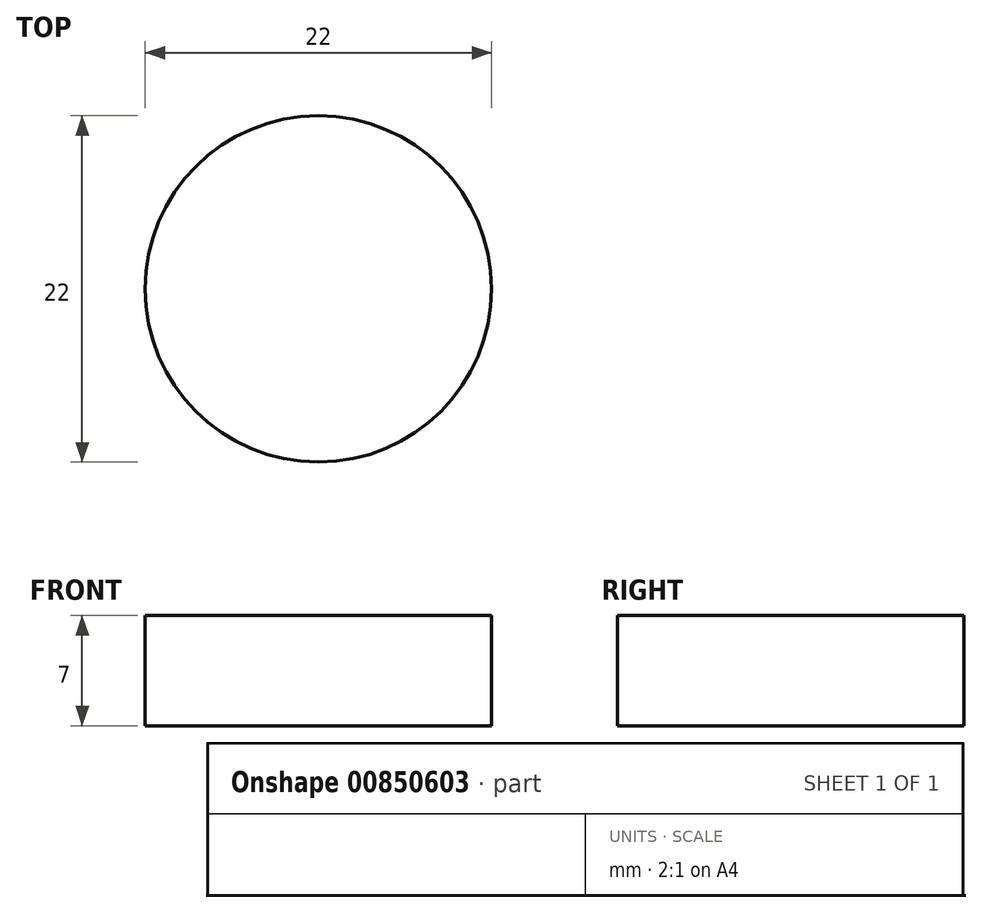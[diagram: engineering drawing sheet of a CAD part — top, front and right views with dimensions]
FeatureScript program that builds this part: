
annotation { "Feature Type Name" : "Feature", "Feature Type Description" : "" }
export const myFeature = defineFeature(function(context is Context, id is Id, definition is map)
    precondition{}
    {
        {
            var Q0;
            Q0=qCreatedBy(makeId("Top.planeOp"),FACE);
            var sketch = newSketch(context, id + "F0", { "sketchPlane" : qUnion([Q0])});
            skCircle(sketch, "E0", {"center": v(2.2, 0) * mm, "radius": 11 * mm});
            skSolve(sketch);
        }
        {
            var Q0;
            Q0 = qSketchRegion(id + "F0", true);
            extrude(context, id + "F1", {"entities" : qUnion([Q0]), "depth" : 7 * mm, "offsetDistance" : 25 * mm});
        }
    });
